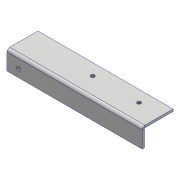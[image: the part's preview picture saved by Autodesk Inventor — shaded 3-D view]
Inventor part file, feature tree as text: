
AUTODESK INVENTOR PART (.ipt)
format: ipt  version: 2016 (Build 200138000, 138)  size: 145,920 bytes
history: native  units: mm
features: sheet_metal_op x4, hole x3, other x3, sketch x2
ambient origin geometry x8: Origin, YZ Plane, XZ Plane, XY Plane, X Axis, Y Axis, Z Axis, Center Point
bodies: Solid1 (feature_tree)
feature tree (12):
  sheet_metal_op  "Face1"
  sheet_metal_op  "Flange1"
  hole  "Hole3"  [1 undecoded]
  hole  "Hole4"  [1 undecoded]
  hole  "Hole5"  [1 undecoded]
  sketch  "Sketch1"  dims[d0=175.0mm d1=40.0mm]
  other  "Plate1"
  sketch  "Sketch2"  dims[d2=3.0mm d3=3.0mm d4=1.5mm d5=6.0mm d6=3.0mm d7=25.0mm d8=90.0deg d9=0.5mm d10=12.0mm d11=3.0mm d12=3.0mm d31=15.0mm d32=29.0mm d33=5.0mm d34=6.0mm d35=4.0mm d36=2.0mm d37=90.0deg d38=3.0mm d39=20.594885mm d40=15.0mm d41=89.0mm d42=5.0mm d43=6.0mm d44=4.0mm d45=2.0mm d46=90.0deg d47=3.0mm d48=20.594885mm d49=15.0mm d50=10.0mm d51=5.0mm d52=6.0mm d53=4.0mm d54=2.0mm d55=90.0deg d56=3.0mm d57=20.594885mm]
  other  "Plate2"
  sheet_metal_op  "Bend1"
  sheet_metal_op  "Corner1"
  other  "Definition1"
note: 3 required parameter values undecoded (feature->parameter linkage not recoverable at this tier; creation-order binding heuristic only, values carry confidence <= 0.55)
